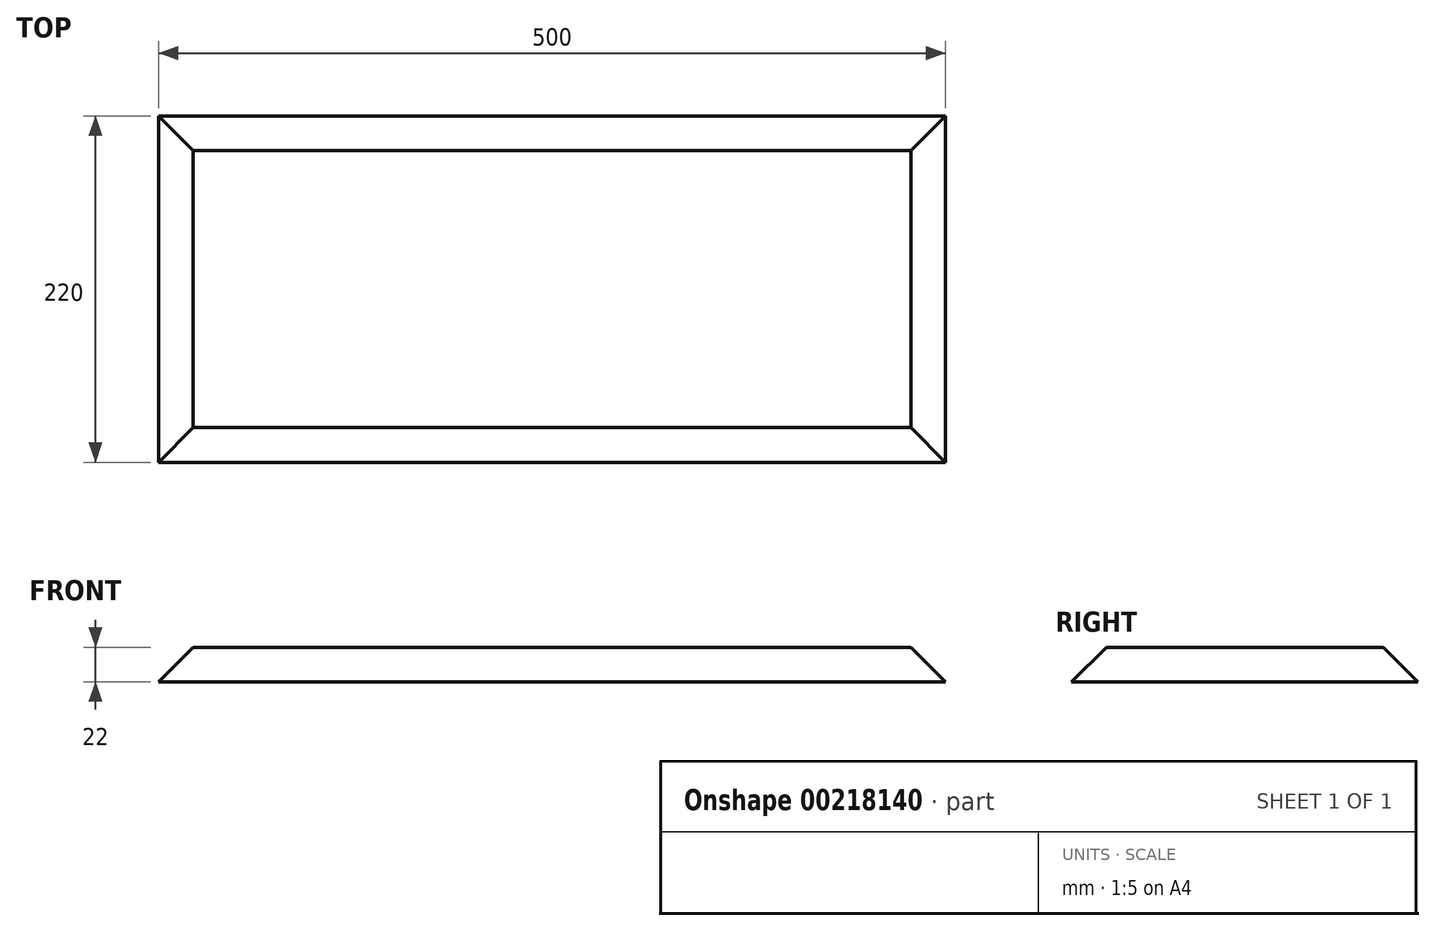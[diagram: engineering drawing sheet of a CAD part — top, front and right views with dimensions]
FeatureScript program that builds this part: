
annotation { "Feature Type Name" : "Feature", "Feature Type Description" : "" }
export const myFeature = defineFeature(function(context is Context, id is Id, definition is map)
    precondition{}
    {
        {
            var Q0;
            Q0=qCreatedBy(makeId("Top.planeOp"),FACE);
            var sketch = newSketch(context, id + "F0", { "sketchPlane" : qUnion([Q0])});
            skLineSegment(sketch, "E0.bottom", {"start": v(250, -110) * mm, "end": v(-250, -110) * mm});
            skLineSegment(sketch, "E0.top", {"start": v(250, 110) * mm, "end": v(-250, 110) * mm});
            skLineSegment(sketch, "E0.left", {"start": v(250, -110) * mm, "end": v(250, 110) * mm});
            skLineSegment(sketch, "E0.right", {"start": v(-250, -110) * mm, "end": v(-250, 110) * mm});
            skPoint(sketch, "E0.middle", {"position": v(0, 0) * mm});
            skSolve(sketch);
        }
        {
            var Q0;
            Q0=makeQuery(id+"F0.imprint","IMPRINT",FACE,{"disambiguationData":[TD([[makeQuery(id+"F0.imprint","IMPRINT",EDGE,{"derivedFrom":sQuery(id+"F0.wireOp",EDGE,"E0.bottom")}),-1.0]])]});
            extrude(context, id + "F1", {"entities" : qUnion([Q0]), "depth" : 22 * mm});
        }
        {
            var Q0;
            Q0=makeQuery(id+"F1.opExtrude","CAP_EDGE",EDGE,{"disambiguationData":[OSD([sQuery(id+"F0.wireOp",EDGE,"E0.left")])],"isStart":false});
            var Q1;
            Q1=makeQuery(id+"F1.opExtrude","CAP_EDGE",EDGE,{"disambiguationData":[OSD([sQuery(id+"F0.wireOp",EDGE,"E0.bottom")])],"isStart":false});
            var Q2;
            Q2=makeQuery(id+"F1.opExtrude","CAP_EDGE",EDGE,{"disambiguationData":[OSD([sQuery(id+"F0.wireOp",EDGE,"E0.right")])],"isStart":false});
            var Q3;
            Q3=makeQuery(id+"F1.opExtrude","CAP_EDGE",EDGE,{"disambiguationData":[OSD([sQuery(id+"F0.wireOp",EDGE,"E0.top")])],"isStart":false});
            chamfer(context, id + "F2", {"entities" : qUnion([Q0, Q1, Q2, Q3]), "width" : 22 * mm, "tangentPropagation" : true});
        }
    });
